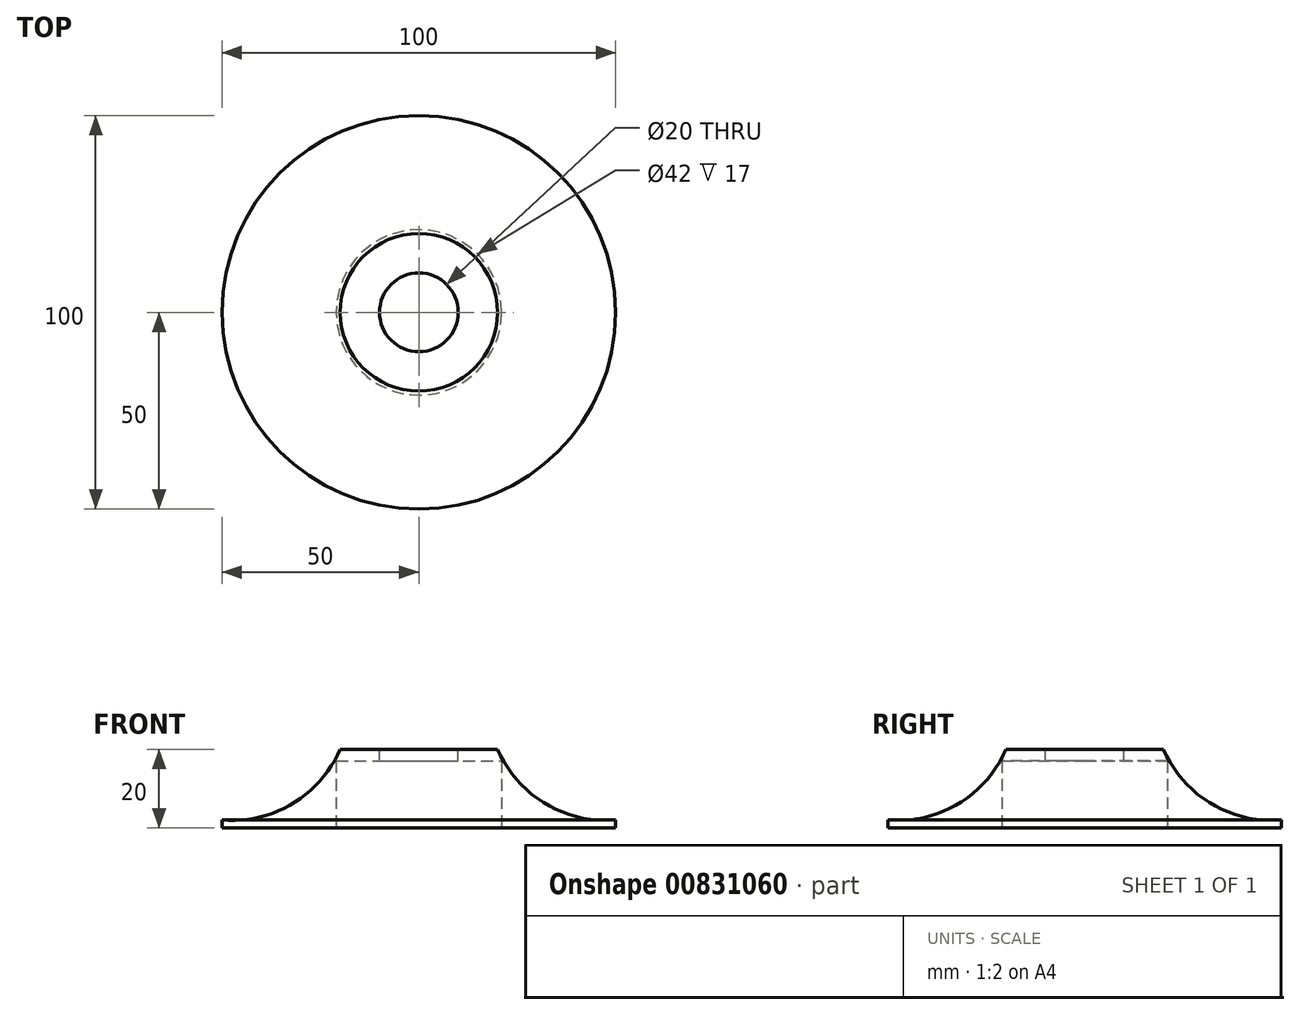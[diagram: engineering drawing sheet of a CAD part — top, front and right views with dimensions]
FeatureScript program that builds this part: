
annotation { "Feature Type Name" : "Feature", "Feature Type Description" : "" }
export const myFeature = defineFeature(function(context is Context, id is Id, definition is map)
    precondition{}
    {
        {
            var Q0;
            Q0=qCreatedBy(makeId("Front.planeOp"),FACE);
            var sketch = newSketch(context, id + "F0", { "sketchPlane" : qUnion([Q0])});
            skLineSegment(sketch, "E0", {"start": v(0, 0) * mm, "end": v(50, 0) * mm});
            skLineSegment(sketch, "E1", {"start": v(0, 0) * mm, "end": v(0, 20) * mm});
            skLineSegment(sketch, "E2", {"start": v(0, 20) * mm, "end": v(20, 20) * mm});
            skLineSegment(sketch, "E3", {"start": v(50, 0) * mm, "end": v(50, 2) * mm});
            skArc(sketch, "E4", {"start": v(20, 20) * mm, "mid": v(32.1, 6.17) * mm, "end": v(50, 2) * mm});
            skSolve(sketch);
        }
        {
            var Q0;
            Q0=makeQuery(id+"F0.imprint","IMPRINT",FACE,{"disambiguationData":[TD([[makeQuery(id+"F0.imprint","IMPRINT",EDGE,{"derivedFrom":sQuery(id+"F0.wireOp",EDGE,"E0")}),1.0]])]});
            var Q1;
            Q1=sQuery(id+"F0.wireOp",EDGE,"E1");
            revolve(context, id + "F1", {"surfaceOperationType" : NewSurfaceOperationType.NEW, "entities" : qUnion([Q0]), "axis" : qUnion([Q1]), "revolveType" : RevolveType.FULL});
        }
        {
            var Q0;
            Q0=makeQuery(id+"F1.opRevolve","SWEPT_FACE",FACE,{"disambiguationData":[OSD([sQuery(id+"F0.wireOp",EDGE,"E2")])]});
            var sketch = newSketch(context, id + "F2", { "sketchPlane" : qUnion([Q0])});
            skCircle(sketch, "E5", {"center": v(0, 0) * mm, "radius": 10 * mm});
            skSolve(sketch);
        }
        {
            var Q0;
            Q0=makeQuery(id+"F2.imprint","IMPRINT",FACE,{"disambiguationData":[TD([[makeQuery(id+"F2.imprint","IMPRINT",EDGE,{"derivedFrom":sQuery(id+"F2.wireOp",EDGE,"E5")}),1.0]])]});
            extrude(context, id + "F3", {"entities" : qUnion([Q0]), "operationType" : NewBodyOperationType.REMOVE, "endBound" : BoundingType.THROUGH_ALL, "oppositeDirection" : true, "depth" : 25 * mm, "offsetDistance" : 25 * mm});
        }
        {
            var Q0;
            Q0=makeQuery(id+"F1.opRevolve","SWEPT_FACE",FACE,{"disambiguationData":[OSD([sQuery(id+"F0.wireOp",EDGE,"E0")])]});
            var sketch = newSketch(context, id + "F4", { "sketchPlane" : qUnion([Q0])});
            skCircle(sketch, "E6", {"center": v(0, 0) * mm, "radius": 21 * mm});
            skCircle(sketch, "E7", {"center": v(0, 0) * mm, "radius": 8 * mm});
            skSolve(sketch);
        }
        {
            var Q0;
            Q0=makeQuery(id+"F4.imprint","IMPRINT",FACE,{"disambiguationData":[TD([[makeQuery(id+"F4.imprint","IMPRINT",EDGE,{"derivedFrom":sQuery(id+"F4.wireOp",EDGE,"E6")}),1.0]])]});
            extrude(context, id + "F5", {"entities" : qUnion([Q0]), "operationType" : NewBodyOperationType.REMOVE, "oppositeDirection" : true, "depth" : 17 * mm, "offsetDistance" : 25 * mm});
        }
    });
